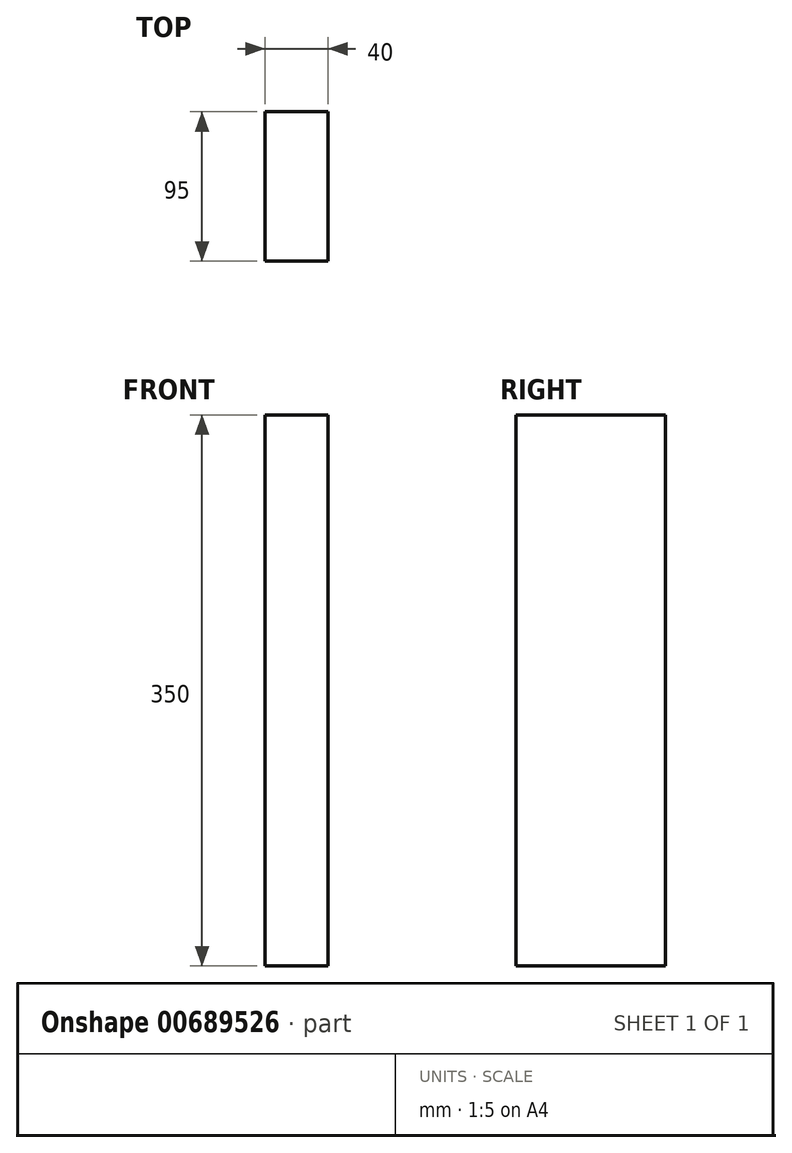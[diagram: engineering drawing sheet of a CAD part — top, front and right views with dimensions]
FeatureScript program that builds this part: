
annotation { "Feature Type Name" : "Feature", "Feature Type Description" : "" }
export const myFeature = defineFeature(function(context is Context, id is Id, definition is map)
    precondition{}
    {
        {
            var Q0;
            Q0=qCreatedBy(makeId("Top.planeOp"),FACE);
            var sketch = newSketch(context, id + "F0", { "sketchPlane" : qUnion([Q0])});
            skLineSegment(sketch, "E0.bottom", {"start": v(-47.53, 91.1) * mm, "end": v(-7.53, 91.1) * mm});
            skLineSegment(sketch, "E0.top", {"start": v(-47.53, -3.9) * mm, "end": v(-7.53, -3.9) * mm});
            skLineSegment(sketch, "E0.left", {"start": v(-47.53, 91.1) * mm, "end": v(-47.53, -3.9) * mm});
            skLineSegment(sketch, "E0.right", {"start": v(-7.53, 91.1) * mm, "end": v(-7.53, -3.9) * mm});
            skSolve(sketch);
        }
        {
            var Q0;
            Q0=makeQuery(id+"F0.imprint","IMPRINT",FACE,{"disambiguationData":[TD([[makeQuery(id+"F0.imprint","IMPRINT",EDGE,{"derivedFrom":sQuery(id+"F0.wireOp",EDGE,"E0.bottom")}),-1.0]])]});
            extrude(context, id + "F1", {"entities" : qUnion([Q0]), "depth" : 350 * mm, "offsetDistance" : 25 * mm});
        }
    });
